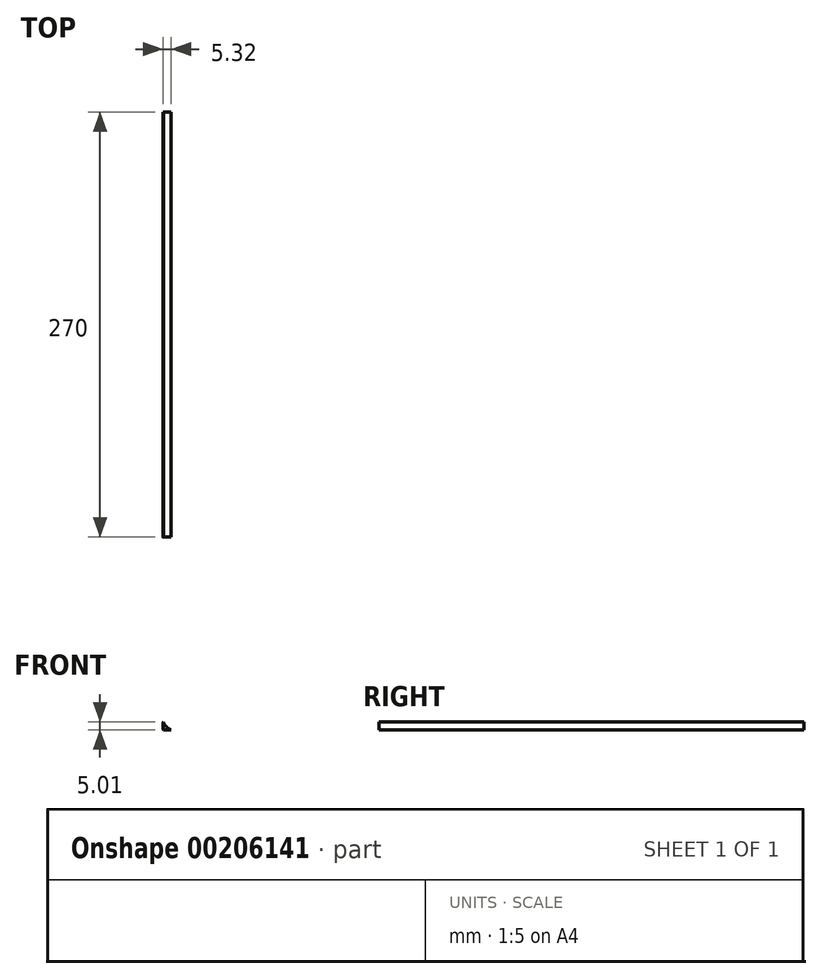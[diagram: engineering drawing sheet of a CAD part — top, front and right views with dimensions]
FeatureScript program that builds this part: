
annotation { "Feature Type Name" : "Feature", "Feature Type Description" : "" }
export const myFeature = defineFeature(function(context is Context, id is Id, definition is map)
    precondition{}
    {
        {
            var Q0;
            Q0=qCreatedBy(makeId("Front.planeOp"),FACE);
            var sketch = newSketch(context, id + "F0", { "sketchPlane" : qUnion([Q0])});
            skLineSegment(sketch, "E0", {"start": v(0, 0) * mm, "end": v(0, 0) * mm});
            skPoint(sketch, "E1.end.orphan", {"position": v(-4.91, 0.07) * mm});
            skArc(sketch, "E2", {"start": v(-5.01, 0) * mm, "mid": v(-2.5, -0.31) * mm, "end": v(0, 0) * mm});
            skLineSegment(sketch, "E3", {"start": v(0, 0) * mm, "end": v(0, 5) * mm});
            skArc(sketch, "E4", {"start": v(-5.01, 0) * mm, "mid": v(-1.85, 1.84) * mm, "end": v(0, 5) * mm});
            skSolve(sketch);
        }
        {
            var Q0;
            {var subQ0=sQuery(id+"F0.wireOp",EDGE,"E4");Q0=makeQuery(id+"F0.imprint","IMPRINT",FACE,{"disambiguationData":[TD([[makeQuery(id+"F0.imprint","IMPRINT",EDGE,{"derivedFrom":subQ0}),-1.0]])]});}
            extrude(context, id + "F1", {"entities" : qUnion([Q0]), "offsetDistance" : 25 * mm, "depth" : 270 * mm});
        }
        {
            var Q0;
            Q0=makeQuery(id+"F1.opExtrude","SWEPT_BODY",BODY,{"disambiguationData":[OSD([sQuery(id+"F0.wireOp",EDGE,"E2"),sQuery(id+"F0.wireOp",EDGE,"E3"),sQuery(id+"F0.wireOp",EDGE,"E4")])]});
            var Q1;
            Q1=makeQuery(id+"F1.opExtrude","SWEPT_EDGE",EDGE,{"disambiguationData":[OSD([sQuery(id+"F0.wireOp",EDGE,"E2"),sQuery(id+"F0.wireOp",EDGE,"E3")])]});
            var Q2;
            Q2=makeQuery(id+"F1.opExtrude","SWEPT_EDGE",EDGE,{"disambiguationData":[OSD([sQuery(id+"F0.wireOp",EDGE,"E2"),sQuery(id+"F0.wireOp",EDGE,"E3")])]});
            transform(context, id + "F2", {"entities" : qUnion([Q0]), "transformType" : TransformType.ROTATION, "transformAxis" : qUnion([Q2]), "angle" : 90 * degree, "makeCopy" : false});
        }
    });
